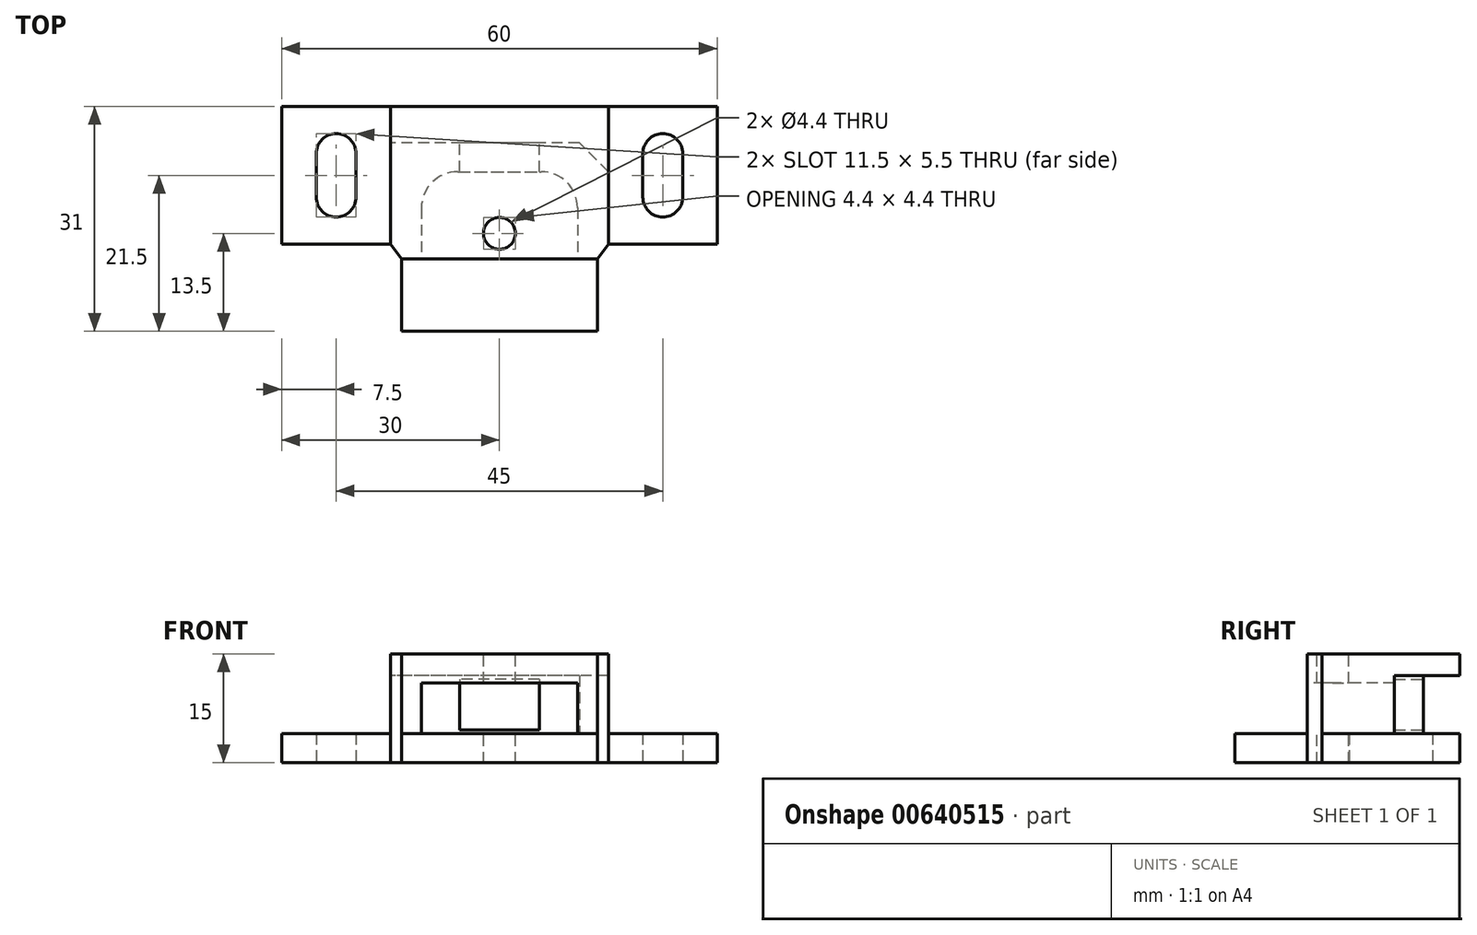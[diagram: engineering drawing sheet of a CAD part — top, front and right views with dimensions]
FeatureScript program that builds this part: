
annotation { "Feature Type Name" : "Feature", "Feature Type Description" : "" }
export const myFeature = defineFeature(function(context is Context, id is Id, definition is map)
    precondition{}
    {
        {
            var Q0;
            Q0=qCreatedBy(makeId("Top.planeOp"),FACE);
            var sketch = newSketch(context, id + "F0", { "sketchPlane" : qUnion([Q0])});
            skLineSegment(sketch, "E0.bottom", {"start": v(-15, 13) * mm, "end": v(15, 13) * mm});
            skLineSegment(sketch, "E0.top", {"start": v(-15, -13) * mm, "end": v(15, -13) * mm});
            skLineSegment(sketch, "E0.left", {"start": v(-15, 13) * mm, "end": v(-15, -13) * mm});
            skLineSegment(sketch, "E0.right", {"start": v(15, 13) * mm, "end": v(15, -13) * mm});
            skSolve(sketch);
        }
        {
            var Q0;
            Q0 = qSketchRegion(id + "F0", true);
            extrude(context, id + "F1", {"entities" : qUnion([Q0]), "depth" : 15 * mm, "offsetDistance" : 25 * mm});
        }
        {
            var Q0;
            Q0=makeQuery(id+"F1.opExtrude","SWEPT_FACE",FACE,{"disambiguationData":[OSD([sQuery(id+"F0.wireOp",EDGE,"E0.top")])]});
            var sketch = newSketch(context, id + "F2", { "sketchPlane" : qUnion([Q0])});
            skLineSegment(sketch, "E1.bottom", {"start": v(-10.75, 11) * mm, "end": v(10.75, 11) * mm});
            skLineSegment(sketch, "E1.top", {"start": v(-10.75, 4) * mm, "end": v(10.75, 4) * mm});
            skLineSegment(sketch, "E1.left", {"start": v(-10.75, 11) * mm, "end": v(-10.75, 4) * mm});
            skLineSegment(sketch, "E1.right", {"start": v(10.75, 11) * mm, "end": v(10.75, 4) * mm});
            skSolve(sketch);
        }
        {
            var Q0;
            Q0=makeQuery(id+"F1.opExtrude","SWEPT_EDGE",EDGE,{"disambiguationData":[OSD([sQuery(id+"F0.wireOp",EDGE,"E0.top"),sQuery(id+"F0.wireOp",EDGE,"E0.left")])]});
            var Q1;
            Q1=makeQuery(id+"F1.opExtrude","SWEPT_EDGE",EDGE,{"disambiguationData":[OSD([sQuery(id+"F0.wireOp",EDGE,"E0.top"),sQuery(id+"F0.wireOp",EDGE,"E0.right")])]});
            chamfer(context, id + "F3", {"entities" : qUnion([Q0, Q1]), "chamferType" : ChamferType.TWO_OFFSETS, "width1" : 1.5 * mm, "oppositeDirection" : false, "width2" : 2 * mm, "tangentPropagation" : true});
        }
        {
            var Q0;
            Q0=makeQuery(id+"F1.opExtrude","SWEPT_FACE",FACE,{"disambiguationData":[OSD([sQuery(id+"F0.wireOp",EDGE,"E0.left")])]});
            var sketch = newSketch(context, id + "F4", { "sketchPlane" : qUnion([Q0])});
            skLineSegment(sketch, "E2", {"start": v(-13, 0) * mm, "end": v(-8, 0) * mm});
            skLineSegment(sketch, "E3", {"start": v(-8, 0) * mm, "end": v(-8, 4) * mm});
            skLineSegment(sketch, "E4", {"start": v(-8, 4) * mm, "end": v(-3, 4) * mm});
            skLineSegment(sketch, "E5", {"start": v(-3, 4) * mm, "end": v(-3, 12) * mm});
            skLineSegment(sketch, "E6", {"start": v(-3, 12) * mm, "end": v(-13, 12) * mm});
            skLineSegment(sketch, "E7", {"start": v(-13, 12) * mm, "end": v(-13, 0) * mm});
            skSolve(sketch);
        }
        {
            var Q0;
            Q0 = qSketchRegion(id + "F4", true);
            extrude(context, id + "F5", {"entities" : qUnion([Q0]), "operationType" : NewBodyOperationType.REMOVE, "endBound" : BoundingType.THROUGH_ALL, "oppositeDirection" : true, "depth" : 25 * mm, "offsetDistance" : 25 * mm});
        }
        {
            var Q0;
            Q0=makeQuery(id+"F5.boolean.opBoolean","COPY",EDGE,{"derivedFrom":makeQuery(id+"F5.opExtrude","CAP_EDGE",EDGE,{"disambiguationData":[OSD([sQuery(id+"F4.wireOp",EDGE,"E5")])],"isStart":true})});
            var Q1;
            Q1=makeQuery(id+"F5.boolean.opBoolean","INTERSECT",EDGE,{"derivedFrom":[makeQuery(id+"F1.opExtrude","SWEPT_FACE",FACE,{"disambiguationData":[OSD([sQuery(id+"F0.wireOp",EDGE,"E0.right")])]}),makeQuery(id+"F5.opExtrude","SWEPT_FACE",FACE,{"disambiguationData":[OSD([sQuery(id+"F4.wireOp",EDGE,"E5")])]})]});
            chamfer(context, id + "F6", {"entities" : qUnion([Q0, Q1]), "width" : 4 * mm, "tangentPropagation" : true});
        }
        {
            var Q0;
            Q0 = qSketchRegion(id + "F2", true);
            extrude(context, id + "F7", {"entities" : qUnion([Q0]), "operationType" : NewBodyOperationType.REMOVE, "oppositeDirection" : true, "depth" : 12 * mm, "offsetDistance" : 25 * mm});
        }
        {
            var Q0;
            Q0=makeQuery(id+"F5.boolean.opBoolean","COPY",FACE,{"derivedFrom":makeQuery(id+"F5.opExtrude","SWEPT_FACE",FACE,{"disambiguationData":[OSD([sQuery(id+"F4.wireOp",EDGE,"E5")])]})});
            var sketch = newSketch(context, id + "F8", { "sketchPlane" : qUnion([Q0])});
            skLineSegment(sketch, "E8.bottom", {"start": v(-5.5, 11.5) * mm, "end": v(5.5, 11.5) * mm});
            skLineSegment(sketch, "E8.top", {"start": v(-5.5, 4.5) * mm, "end": v(5.5, 4.5) * mm});
            skLineSegment(sketch, "E8.left", {"start": v(-5.5, 11.5) * mm, "end": v(-5.5, 4.5) * mm});
            skLineSegment(sketch, "E8.right", {"start": v(5.5, 11.5) * mm, "end": v(5.5, 4.5) * mm});
            skSolve(sketch);
        }
        {
            var Q0;
            Q0 = qSketchRegion(id + "F8", true);
            extrude(context, id + "F9", {"entities" : qUnion([Q0]), "operationType" : NewBodyOperationType.REMOVE, "oppositeDirection" : true, "depth" : 4 * mm, "offsetDistance" : 25 * mm});
        }
        {
            var Q0;
            Q0=makeQuery(id+"F7.boolean.opBoolean","COPY",EDGE,{"derivedFrom":makeQuery(id+"F7.opExtrude","CAP_EDGE",EDGE,{"disambiguationData":[OSD([sQuery(id+"F2.wireOp",EDGE,"E1.left")])],"isStart":false})});
            fillet(context, id + "F10", {"entities" : qUnion([Q0]), "radius" : 5 * mm, "tangentPropagation" : true, "allowEdgeOverflow" : false});
        }
        {
            var Q0;
            Q0=makeQuery(id+"F7.boolean.opBoolean","COPY",EDGE,{"derivedFrom":makeQuery(id+"F7.opExtrude","CAP_EDGE",EDGE,{"disambiguationData":[OSD([sQuery(id+"F2.wireOp",EDGE,"E1.right")])],"isStart":false})});
            fillet(context, id + "F11", {"entities" : qUnion([Q0]), "radius" : 5 * mm, "tangentPropagation" : true, "allowEdgeOverflow" : false});
        }
        {
            var Q0;
            Q0=makeQuery(id+"F1.opExtrude","CAP_FACE",FACE,{"disambiguationData":[OSD([sQuery(id+"F0.wireOp",EDGE,"E0.bottom"),sQuery(id+"F0.wireOp",EDGE,"E0.top"),sQuery(id+"F0.wireOp",EDGE,"E0.left"),sQuery(id+"F0.wireOp",EDGE,"E0.right")])],"isStart":false});
            var sketch = newSketch(context, id + "F12", { "sketchPlane" : qUnion([Q0])});
            skLineSegment(sketch, "E9.bottom", {"start": v(15, 13) * mm, "end": v(-15, 13) * mm});
            skLineSegment(sketch, "E9.top", {"start": v(15, 8) * mm, "end": v(-15, 8) * mm});
            skLineSegment(sketch, "E9.left", {"start": v(15, 13) * mm, "end": v(15, 8) * mm});
            skLineSegment(sketch, "E9.right", {"start": v(-15, 13) * mm, "end": v(-15, 8) * mm});
            skSolve(sketch);
        }
        {
            var Q0;
            Q0 = qSketchRegion(id + "F12", true);
            extrude(context, id + "F13", {"entities" : qUnion([Q0]), "operationType" : NewBodyOperationType.REMOVE, "endBound" : BoundingType.THROUGH_ALL, "oppositeDirection" : true, "depth" : 25 * mm, "offsetDistance" : 25 * mm});
        }
        {
            var Q0;
            Q0=makeQuery(id+"F1.opExtrude","CAP_FACE",FACE,{"disambiguationData":[OSD([sQuery(id+"F0.wireOp",EDGE,"E0.bottom"),sQuery(id+"F0.wireOp",EDGE,"E0.top"),sQuery(id+"F0.wireOp",EDGE,"E0.left"),sQuery(id+"F0.wireOp",EDGE,"E0.right")])],"isStart":false});
            var sketch = newSketch(context, id + "F14", { "sketchPlane" : qUnion([Q0])});
            skPoint(sketch, "E10", {"position": v(0, -9.5) * mm});
            skPoint(sketch, "E10.positionSnap0", {"position": v(0, -13) * mm});
            skSolve(sketch);
        }
        {
            var Q0;
            Q0=sQuery(id+"F14.wireOp",VERTEX,"E10");
            var Q1;
            Q1=makeQuery(id+"F1.opExtrude","SWEPT_BODY",BODY,{"disambiguationData":[OSD([sQuery(id+"F0.wireOp",EDGE,"E0.bottom"),sQuery(id+"F0.wireOp",EDGE,"E0.top"),sQuery(id+"F0.wireOp",EDGE,"E0.left"),sQuery(id+"F0.wireOp",EDGE,"E0.right")])]});
            hole(context, id + "F15", {"style" : HoleStyle.SIMPLE, "endStyle" : HoleEndStyle.THROUGH, "standardTappedOrClearance" : lookupTablePath({ "standard" : "ISO", "fit" : "Normal", "size" : "M4", "type" : "Clearance" }), "standardBlindInLast" : lookupTablePath({ "fit" : "Standard", "standard" : "ISO", "size" : "M4", "type" : "Clearance" }), "holeDiameter" : 4.4 * mm, "majorDiameter" : 5 * mm, "isTappedThrough" : true, "tappedDepth" : 12 * mm, "tapClearance" : 3, "locations" : qUnion([Q0]), "scope" : qUnion([Q1])});
        }
        {
            var Q0;
            Q0=makeQuery(id+"F1.opExtrude","CAP_FACE",FACE,{"disambiguationData":[OSD([sQuery(id+"F0.wireOp",EDGE,"E0.bottom"),sQuery(id+"F0.wireOp",EDGE,"E0.top"),sQuery(id+"F0.wireOp",EDGE,"E0.left"),sQuery(id+"F0.wireOp",EDGE,"E0.right")])],"isStart":true});
            var sketch = newSketch(context, id + "F16", { "sketchPlane" : qUnion([Q0])});
            skLineSegment(sketch, "E11.bottom", {"start": v(-13.5, 13) * mm, "end": v(13.5, 13) * mm});
            skLineSegment(sketch, "E11.top", {"start": v(-13.5, 23) * mm, "end": v(13.5, 23) * mm});
            skLineSegment(sketch, "E11.left", {"start": v(-13.5, 13) * mm, "end": v(-13.5, 23) * mm});
            skLineSegment(sketch, "E11.right", {"start": v(13.5, 13) * mm, "end": v(13.5, 23) * mm});
            skLineSegment(sketch, "E12.bottom", {"start": v(15, 11) * mm, "end": v(30, 11) * mm});
            skLineSegment(sketch, "E12.top", {"start": v(15, -8) * mm, "end": v(30, -8) * mm});
            skLineSegment(sketch, "E12.left", {"start": v(15, 11) * mm, "end": v(15, -8) * mm});
            skLineSegment(sketch, "E12.right", {"start": v(30, 11) * mm, "end": v(30, -8) * mm});
            skLineSegment(sketch, "E13.MirrorCS", {"start": v(-15, 11) * mm, "end": v(-30, 11) * mm});
            skLineSegment(sketch, "E14.MirrorCS", {"start": v(-30, 11) * mm, "end": v(-30, -8) * mm});
            skLineSegment(sketch, "E15.MirrorCS", {"start": v(-15, -8) * mm, "end": v(-30, -8) * mm});
            skLineSegment(sketch, "E16.MirrorCS", {"start": v(-15, 11) * mm, "end": v(-15, -8) * mm});
            skLineSegment(sketch, "E17.left", {"start": v(19.75, 4.5) * mm, "end": v(19.75, -1.5) * mm});
            skLineSegment(sketch, "E17.right", {"start": v(25.25, 4.5) * mm, "end": v(25.25, -1.5) * mm});
            skArc(sketch, "E18", {"start": v(19.75, 4.5) * mm, "mid": v(22.5, 7.25) * mm, "end": v(25.25, 4.5) * mm});
            skArc(sketch, "E19", {"start": v(19.75, -1.5) * mm, "mid": v(22.5, -4.25) * mm, "end": v(25.25, -1.5) * mm});
            skLineSegment(sketch, "E20.MirrorCS", {"start": v(-19.75, 4.5) * mm, "end": v(-19.75, -1.5) * mm});
            skArc(sketch, "E21.MirrorCS", {"start": v(-19.75, 4.5) * mm, "mid": v(-22.5, 7.25) * mm, "end": v(-25.25, 4.5) * mm});
            skLineSegment(sketch, "E22.MirrorCS", {"start": v(-25.25, 4.5) * mm, "end": v(-25.25, -1.5) * mm});
            skArc(sketch, "E23.MirrorCS", {"start": v(-19.75, -1.5) * mm, "mid": v(-22.5, -4.25) * mm, "end": v(-25.25, -1.5) * mm});
            skSolve(sketch);
        }
        {
            var Q0;
            Q0 = qSketchRegion(id + "F16", true);
            extrude(context, id + "F17", {"entities" : qUnion([Q0]), "operationType" : NewBodyOperationType.ADD, "oppositeDirection" : true, "depth" : 4 * mm, "offsetDistance" : 25 * mm});
        }
    });
